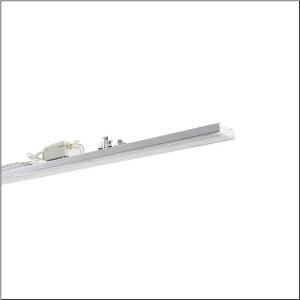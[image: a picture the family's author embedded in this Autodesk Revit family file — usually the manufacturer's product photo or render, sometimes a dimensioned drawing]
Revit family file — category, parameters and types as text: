
# Revit family: licross_21_recessed_mo_52te19cn485g
name_source: partatom
category: Lighting Fixtures
units: mm (PartAtom-declared; Revit-internal decimal feet)

## family parameters
Cut with Voids When Loaded = No
Host = Face
Light Source = No
Part Type = Normal
Room Calculation Point = No
Round Connector Dimension = Use Diameter
Shared = No

## types (1)
- --- (1 x LED, 8870 lm, 49.9 W, 4000K)
    Apparent Load = 50 VA
    CIE Flux Codes = 55 90 98 100 100
    Color Rendering = 80
    Color Temperature = 4000K
    Default Elevation = 1800 mm
    Description = Licross 21 Recessed MO, luminaire insert, of sheet steel, galvanised, coil coated, white, length: 1.500mm, width: 66mm, height: 67mm, LED rated luminous flux: 8.880lm, light colour: 840, SDCM (Standard Deviation of Colour Matching)MacAdam ≤ 3 SDCM (initial), control gear: ON/OFF Multilumen, CLOi, with plug, 5-pole, with phase selection, mains connection: 220..240V, AC, 50/60Hz, start of lifetime: 50W, end of service life: 61W, internal wiring halogen-free, primary light control with lens, of plastic, primary optical cover: cover, of PMMA, light emission: direct distribution, primary light characteristic: double asymmetric, protection rating (complete): IP54, insulation class (complete): insulation class I (protective earthing), certification: CE, ENEC, VDE, UKCA, protection symbol: D if used in an environment with non-conductive dust loads with corresponding accessories, impact resistance: IK06, permissible ambient temperature for indoor applications: -35..+40°C, corresponds to IFS (International Featured Standards) requirements for safety and quality in the food industry, reducing of maximum allowable ambient temperature of 5°C with ceiling mounting, LABS conformity tested according to VDMA 24364:2018-05, The light source and the operating device comply with the requirements of the Ecodesign Regulation (EU) 2019/2020 and are replaceable in accordance with this regulation, packaging unit: 1 piece
    Height = 58 mm
    Lamp = 1 x LED
    Lamp Light Flux = 8870 lm
    Lamp Power = 49.9 W
    Lamp count = 1
    Length = 1500 mm
    Luminous efficacy = 178 lm/W
    Manufacturer = Siteco
    ModVariant = No
    Model = 52TE19CN485G
    Mounting Place = Ceiling
    Mounting Type = Pendant
    Number of Poles = 1
    OnlyDefault = Yes
    Power Factor = 1
    Product Name = Licross 21 Recessed MO
    Product group = luminaire insert | ceiling pendant
    ProductGroupID = 901
    Protection Class = Protection class I
    Protection Degree = IP 54
    RLX_Detail_Level = 1
    RLX_Emergency_Light_Flux = 0 lm
    RLX_Emergency_Type = 0
    RLX_Emergency_Type_DB = No
    RlxData = <blob elided: 22593 chars, md5=6e32a06a>
    Socket = socket
    Standby Power = 0 W
    System Light Flux = 8870 lm
    System Power = 50 W
    Type Comments = factory setting: luminous flux: 100 % | (A | C | E) | 116 mA
    Type Image = l_1296930.jpg
    URL = http://relux.com
    VarID = @adj_112301
    Voltage = 0 V
    Weight = 0.00 kg
    Width = 66 mm

## geometry (parser evidence)
native form markers: Blend x4, Sweep x10
no freeform markers — native parametric forms only
